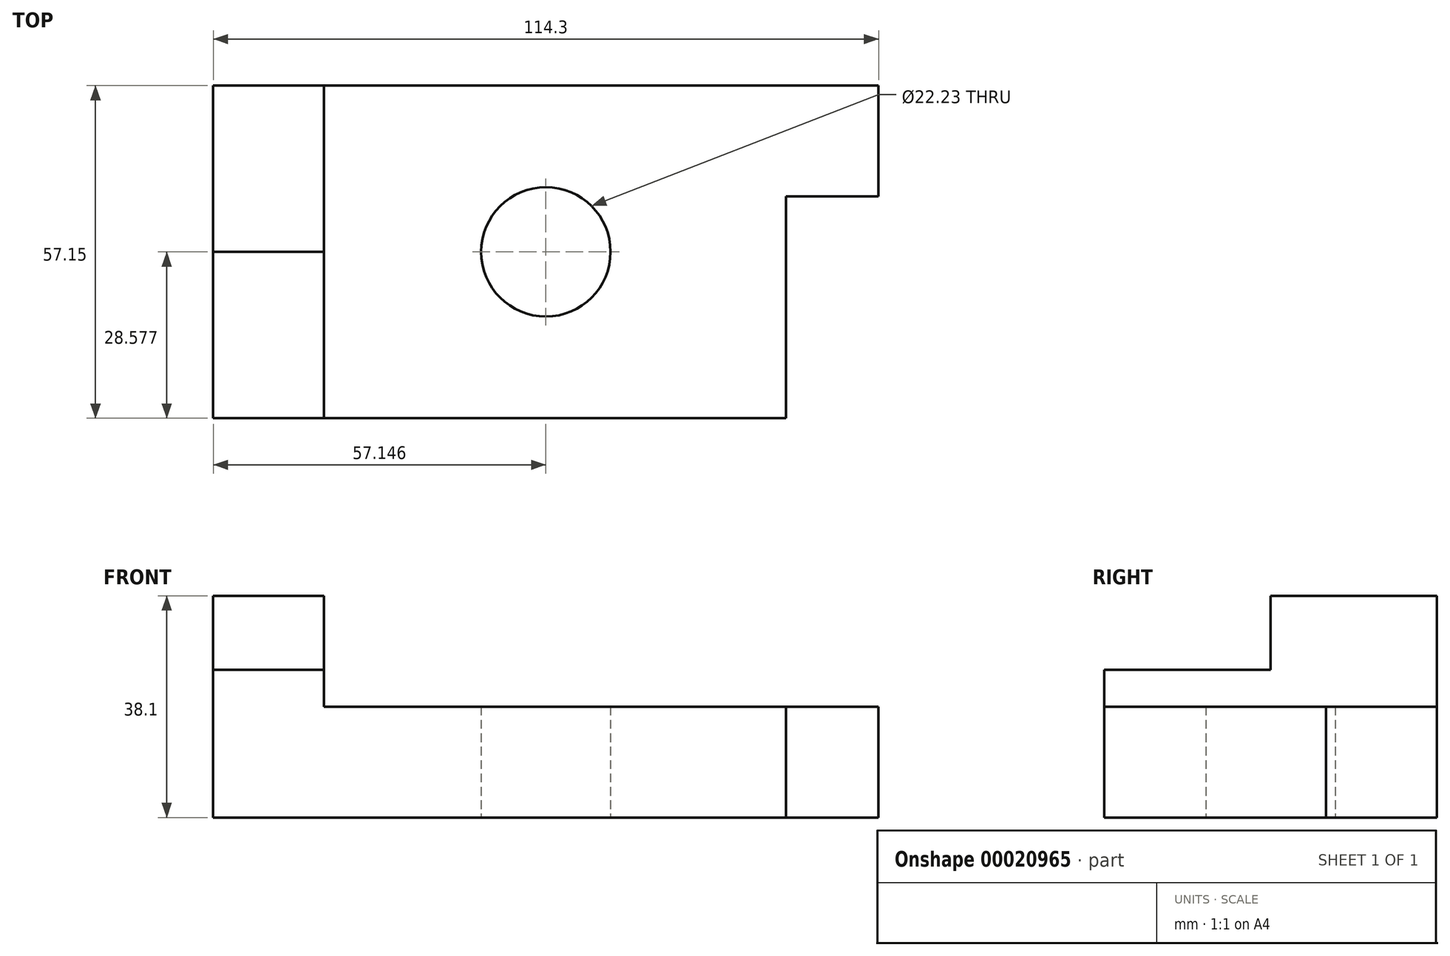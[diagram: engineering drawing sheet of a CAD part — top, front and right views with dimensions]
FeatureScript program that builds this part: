
annotation { "Feature Type Name" : "Feature", "Feature Type Description" : "" }
export const myFeature = defineFeature(function(context is Context, id is Id, definition is map)
    precondition{}
    {
        {
            var Q0;
            Q0=qCreatedBy(makeId("Top.planeOp"),FACE);
            var sketch = newSketch(context, id + "F0", { "sketchPlane" : qUnion([Q0])});
            skLineSegment(sketch, "E0.bottom", {"start": v(-57.46, 22.92) * mm, "end": v(56.84, 22.92) * mm});
            skLineSegment(sketch, "E0.top", {"start": v(-57.46, -34.23) * mm, "end": v(40.96, -34.23) * mm});
            skLineSegment(sketch, "E0.left", {"start": v(-57.46, 22.92) * mm, "end": v(-57.46, -34.23) * mm});
            skLineSegment(sketch, "E0.right", {"start": v(56.84, 22.92) * mm, "end": v(56.84, 3.87) * mm});
            skLineSegment(sketch, "E1.top", {"start": v(56.84, 3.87) * mm, "end": v(40.96, 3.87) * mm});
            skLineSegment(sketch, "E1.right", {"start": v(40.96, -34.23) * mm, "end": v(40.96, 3.87) * mm});
            skLineSegment(sketch, "E2.bottom", {"start": v(-57.46, 22.92) * mm, "end": v(-38.41, 22.92) * mm});
            skLineSegment(sketch, "E2.top", {"start": v(-57.46, -34.23) * mm, "end": v(-38.41, -34.23) * mm});
            skLineSegment(sketch, "E2.right", {"start": v(-38.41, 22.92) * mm, "end": v(-38.41, -34.23) * mm});
            skLineSegment(sketch, "E3.top", {"start": v(-57.46, -5.65) * mm, "end": v(-38.41, -5.65) * mm});
            skLineSegment(sketch, "E3.left", {"start": v(-57.46, 22.92) * mm, "end": v(-57.46, -5.65) * mm});
            skLineSegment(sketch, "E3.right", {"start": v(-38.41, 22.92) * mm, "end": v(-38.41, -5.65) * mm});
            skLineSegment(sketch, "E4.bottom", {"start": v(56.84, 22.92) * mm, "end": v(-0.31, 22.92) * mm});
            skCircle(sketch, "E5", {"center": v(-0.31, -5.65) * mm, "radius": 11.11 * mm});
            skSolve(sketch);
        }
        {
            var Q0;
            Q0 = qSketchRegion(id + "F0", true);
            extrude(context, id + "F1", {"entities" : qUnion([Q0]), "depth" : 19.05 * mm});
        }
        {
            var Q0;
            Q0=makeQuery(id+"F1.opExtrude","CAP_FACE",FACE,{"disambiguationData":[OSD([sQuery(id+"F0.wireOp",EDGE,"E0.bottom"),sQuery(id+"F0.wireOp",EDGE,"E0.top"),sQuery(id+"F0.wireOp",EDGE,"E1.top"),sQuery(id+"F0.wireOp",EDGE,"E1.right"),sQuery(id+"F0.wireOp",EDGE,"E2.top"),sQuery(id+"F0.wireOp",EDGE,"E0.left"),sQuery(id+"F0.wireOp",EDGE,"E2.bottom"),sQuery(id+"F0.wireOp",EDGE,"E3.left"),sQuery(id+"F0.wireOp",EDGE,"E4.bottom"),sQuery(id+"F0.wireOp",EDGE,"E0.right"),sQuery(id+"F0.wireOp",EDGE,"E5")])],"isStart":false});
            var sketch = newSketch(context, id + "F2", { "sketchPlane" : qUnion([Q0])});
            skLineSegment(sketch, "E6.bottom", {"start": v(-57.46, 22.92) * mm, "end": v(-38.41, 22.92) * mm});
            skLineSegment(sketch, "E6.top", {"start": v(-57.46, -34.23) * mm, "end": v(-38.41, -34.23) * mm});
            skLineSegment(sketch, "E6.left", {"start": v(-57.46, 22.92) * mm, "end": v(-57.46, -34.23) * mm});
            skLineSegment(sketch, "E6.right", {"start": v(-38.41, 22.92) * mm, "end": v(-38.41, -34.23) * mm});
            skSolve(sketch);
        }
        {
            var Q0;
            Q0=makeQuery(id+"F2.imprint","IMPRINT",FACE,{"disambiguationData":[TD([[makeQuery(id+"F2.imprint","IMPRINT",EDGE,{"derivedFrom":sQuery(id+"F2.wireOp",EDGE,"E6.bottom")}),-1.0]])]});
            extrude(context, id + "F3", {"entities" : qUnion([Q0]), "operationType" : NewBodyOperationType.ADD, "depth" : 6.35 * mm});
        }
        {
            var Q0;
            Q0=makeQuery(id+"F3.opExtrude","CAP_FACE",FACE,{"disambiguationData":[OSD([sQuery(id+"F2.wireOp",EDGE,"E6.bottom"),sQuery(id+"F2.wireOp",EDGE,"E6.top"),sQuery(id+"F2.wireOp",EDGE,"E6.left"),sQuery(id+"F2.wireOp",EDGE,"E6.right")])],"isStart":false});
            var sketch = newSketch(context, id + "F4", { "sketchPlane" : qUnion([Q0])});
            skLineSegment(sketch, "E7.bottom", {"start": v(-57.46, 22.92) * mm, "end": v(-38.41, 22.92) * mm});
            skLineSegment(sketch, "E7.top", {"start": v(-57.46, -5.65) * mm, "end": v(-38.41, -5.65) * mm});
            skLineSegment(sketch, "E7.left", {"start": v(-57.46, 22.92) * mm, "end": v(-57.46, -5.65) * mm});
            skLineSegment(sketch, "E7.right", {"start": v(-38.41, 22.92) * mm, "end": v(-38.41, -5.65) * mm});
            skSolve(sketch);
        }
        {
            var Q0;
            Q0 = qSketchRegion(id + "F4", true);
            extrude(context, id + "F5", {"entities" : qUnion([Q0]), "operationType" : NewBodyOperationType.ADD, "depth" : 12.7 * mm});
        }
    });
